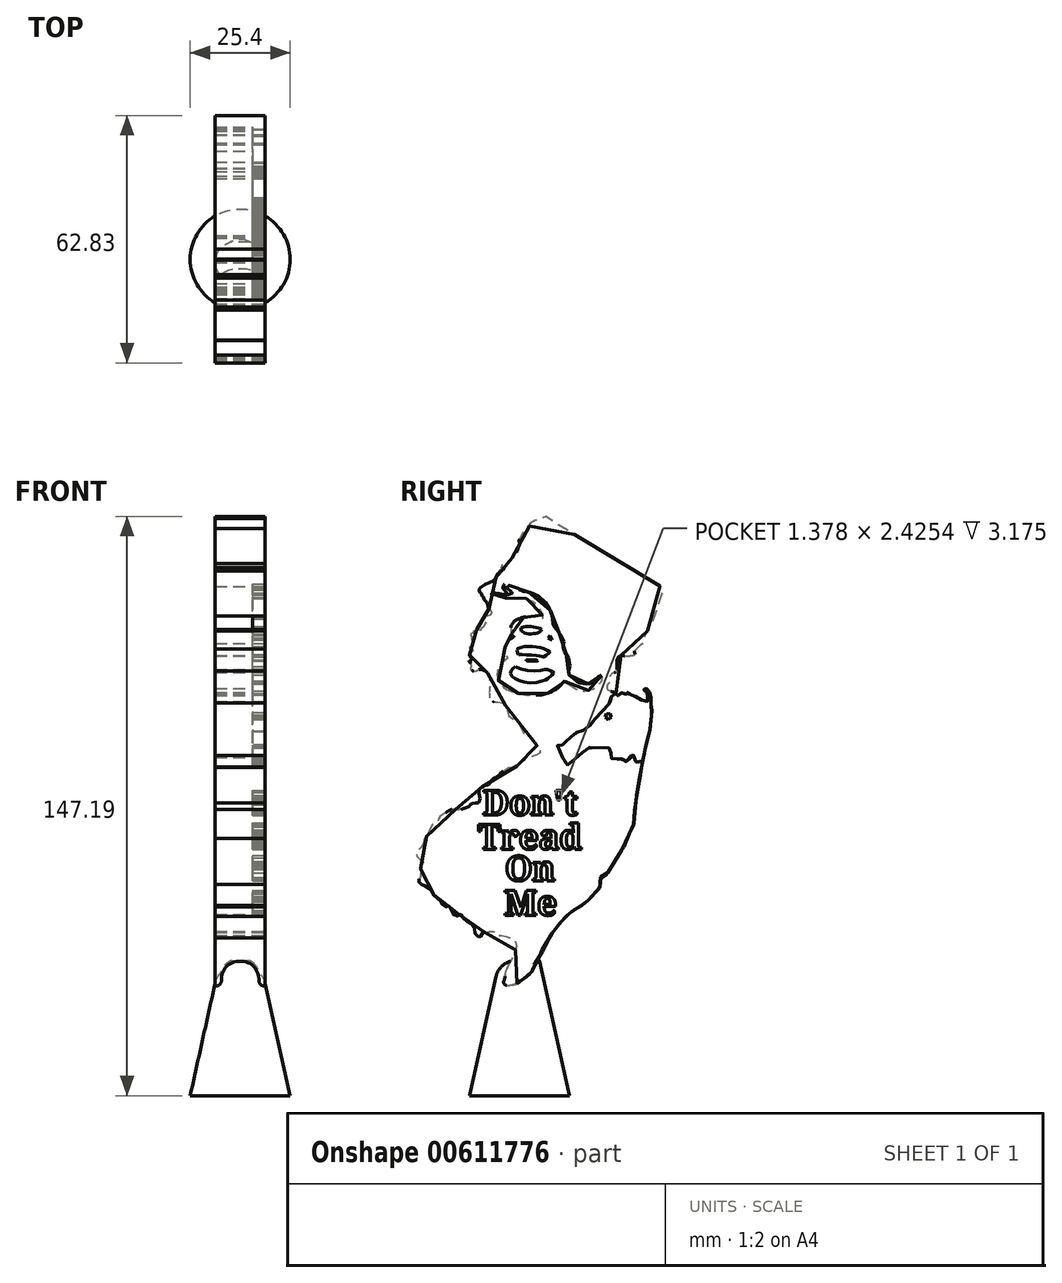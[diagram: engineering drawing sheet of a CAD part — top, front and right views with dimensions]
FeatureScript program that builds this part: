
annotation { "Feature Type Name" : "Feature", "Feature Type Description" : "" }
export const myFeature = defineFeature(function(context is Context, id is Id, definition is map)
    precondition{}
    {
        {
            var Q0;
            Q0=qCreatedBy(makeId("Right.planeOp"),FACE);
            var sketch = newSketch(context, id + "F0", { "sketchPlane" : qUnion([Q0])});
            skLineSegment(sketch, "E0", {"start": v(0, 0) * mm, "end": v(0, 31.75) * mm, "construction": true});
            skFitSpline(sketch, "E1", {"points": [v(-0.7, 28.43) * mm, v(0, 29.08) * mm, v(0.84, 29.6) * mm, v(2.15, 30.47) * mm, v(3.1, 31.63) * mm, v(4.2, 34.04) * mm, v(6.01, 36.44) * mm, v(5.65, 36.95) * mm, v(8.32, 41.31) * mm, v(9.58, 43.23) * mm, v(11.1, 44.75) * mm, v(11.86, 45.66) * mm, v(12.67, 46.31) * mm, v(13.5, 47) * mm, v(14.3, 47.4) * mm, v(15.14, 48.06) * mm, v(17, 48.86) * mm, v(17.25, 49.6) * mm, v(17.98, 50.14) * mm, v(21.04, 53.96) * mm, v(21.04, 54.73) * mm, v(20.57, 55.5) * mm, v(20.93, 56) * mm, v(22.02, 56.19) * mm, v(22.57, 56.95) * mm, v(23.74, 58.6) * mm, v(24.36, 59.83) * mm, v(24.98, 61.03) * mm, v(25.96, 62.3) * mm, v(27.42, 65.3) * mm, v(28.07, 67.08) * mm, v(28.7, 68) * mm, v(29.1, 69.92) * mm, v(29.28, 72.84) * mm, v(29.57, 74.3) * mm, v(29.57, 75.6) * mm, v(29.93, 77.14) * mm, v(30.44, 80.56) * mm, v(30.85, 82.31) * mm, v(31.32, 85.37) * mm, v(31.83, 87.6) * mm, v(32.27, 89.63) * mm, v(33.14, 93.06) * mm, v(33.32, 94.7) * mm, v(33.58, 96.92) * mm, v(33.54, 98.56) * mm, v(33.36, 100.24) * mm, v(33.32, 101.88) * mm, v(32.78, 102.82) * mm, v(32.23, 103.4) * mm, v(31.76, 103.44) * mm, v(31.57, 103.04) * mm, v(32.16, 102.57) * mm, v(32.52, 101.77) * mm, v(32.56, 100.64) * mm, v(32.56, 100.2) * mm, v(31.06, 100.5) * mm, v(29.28, 101.55) * mm, v(28.55, 101.7) * mm, v(28, 102.1) * mm, v(27.56, 102.2) * mm, v(27.53, 102.46) * mm, v(27.1, 102.02) * mm, v(25.85, 102.35) * mm, v(25.38, 101.91) * mm, v(24.87, 101.66) * mm, v(24.61, 102.06) * mm, v(23.85, 102.53) * mm, v(22.68, 102.93) * mm, v(22.32, 104.17) * mm, v(23.15, 105.41) * mm, v(23.15, 106.32) * mm, v(23.04, 106.69) * mm, v(23.88, 107.52) * mm, v(24.47, 107.6) * mm, v(24.72, 108.29) * mm, v(24.83, 110.95) * mm, v(25.63, 111.79) * mm, v(26.65, 111.75) * mm, v(27.3, 111.71) * mm, v(29.31, 112.08) * mm, v(29.28, 112.44) * mm, v(29.28, 113.1) * mm, v(30.63, 114.08) * mm, v(31.14, 114.88) * mm, v(31.72, 114.88) * mm, v(31.61, 115.47) * mm, v(31.83, 115.98) * mm, v(31.9, 116.74) * mm, v(32.3, 117.83) * mm, v(33.03, 119.1) * mm, v(33.03, 119.44) * mm, v(33.43, 119.7) * mm, v(34.05, 121.11) * mm, v(34.5, 122.39) * mm, v(35.26, 123.96) * mm, v(35.7, 126.21) * mm, v(36.28, 127.93) * mm, v(36.5, 129.38) * mm, v(36.24, 129.35) * mm, v(35, 129.82) * mm, v(25.52, 135.5) * mm, v(25.01, 135.72) * mm, v(18.6, 139.62) * mm, v(17.58, 140.1) * mm, v(16.56, 140.93) * mm, v(15.8, 141.3) * mm, v(10.58, 144.8) * mm, v(9.78, 145.09) * mm, v(6.53, 147.16) * mm, v(6.02, 147.05) * mm, v(5.51, 146.84) * mm, v(5.44, 146.62) * mm, v(4.1, 146.65) * mm, v(3.94, 146.33) * mm, v(3.65, 145.7) * mm, v(2.82, 145.52) * mm, v(2.6, 145.3) * mm, v(2.6, 144.8) * mm, v(2.05, 144.5) * mm, v(1.9, 144.14) * mm, v(1.54, 144.1) * mm, v(0.7, 142.57) * mm, v(0.63, 142.03) * mm, v(0.2, 141.7) * mm, v(-0.16, 140.82) * mm, v(0, 140.4) * mm, v(0, 139.9) * mm, v(-0.3, 139.4) * mm, v(-0.83, 137.9) * mm, v(-1.3, 137.8) * mm, v(-1.43, 137.29) * mm, v(-2.2, 136.32) * mm, v(-2.65, 135.82) * mm, v(-3.19, 135.57) * mm, v(-3.32, 135.32) * mm, v(-3.7, 135.16) * mm, v(-4.25, 135.07) * mm, v(-4.77, 133.97) * mm, v(-4.56, 133.93) * mm, v(-4.1, 134.05) * mm, v(-3.9, 134.18) * mm, v(-3.96, 133.85) * mm, v(-4.56, 133.35) * mm, v(-4.92, 133.3) * mm, v(-5.25, 132.71) * mm, v(-5.62, 132.58) * mm, v(-5.74, 132.27) * mm, v(-6.2, 131.24) * mm, v(-7.13, 130.66) * mm, v(-9.1, 129.7) * mm, v(-9.86, 129.13) * mm, v(-10.27, 128.62) * mm, v(-10.1, 127.85) * mm, v(-9.75, 127.66) * mm, v(-9.58, 127.03) * mm, v(-9.23, 126.81) * mm, v(-9.12, 126.24) * mm, v(-8.09, 124.94) * mm, v(-8.06, 124.13) * mm, v(-7.65, 123.79) * mm, v(-7.11, 122.96) * mm, v(-7.15, 122.42) * mm, v(-7.67, 121.9) * mm, v(-8.41, 121.92) * mm, v(-8.87, 121.56) * mm, v(-8.43, 121) * mm, v(-8.35, 120.5) * mm, v(-8.87, 119.95) * mm, v(-8.9, 119.52) * mm, v(-9.15, 119.04) * mm, v(-9.56, 118.93) * mm, v(-9.86, 118.65) * mm, v(-10.06, 118.18) * mm, v(-10.64, 118.18) * mm, v(-11.1, 118.33) * mm, v(-11.45, 118.35) * mm, v(-11.62, 118.41) * mm, v(-11.77, 118.02) * mm, v(-11.9, 117.48) * mm, v(-12.38, 117.3) * mm, v(-12.5, 116.96) * mm, v(-12.07, 116.23) * mm, v(-12.57, 115) * mm, v(-12.77, 113.95) * mm, v(-12.62, 113.5) * mm, v(-12.12, 113.52) * mm, v(-11.75, 113.28) * mm, v(-12.03, 112.85) * mm, v(-12.55, 112.3) * mm, v(-12.75, 111.87) * mm, v(-12.53, 111.57) * mm, v(-12.33, 111.2) * mm, v(-12.18, 110.83) * mm, v(-12.49, 110.46) * mm, v(-12.83, 110.4) * mm, v(-12.55, 109.97) * mm, v(-12.33, 109.73) * mm, v(-12.42, 108.75) * mm, v(-12.38, 108.25) * mm, v(-11.66, 107.9) * mm, v(-10.84, 108.02) * mm, v(-10.38, 108.28) * mm, v(-9.47, 108.21) * mm, v(-8.67, 107.76) * mm, v(-7.63, 106.52) * mm, v(-7.65, 104.92) * mm, v(-7.37, 104.44) * mm, v(-7.7, 103.31) * mm, v(-7.63, 102.7) * mm, v(-7.72, 102.34) * mm, v(-7.59, 102) * mm, v(-7.54, 100.87) * mm, v(-6.07, 99.85) * mm, v(-5.79, 99.9) * mm, v(-4.94, 100.13) * mm, v(-3.62, 99.28) * mm, v(-3.6, 98.92) * mm, v(-3.2, 98.07) * mm, v(-3.08, 97.25) * mm, v(-2.69, 96.4) * mm, v(-1.63, 95.65) * mm, v(-0.5, 94.97) * mm, v(0.26, 93.7) * mm, v(0.74, 92.44) * mm, v(2.51, 91.33) * mm, v(4.14, 89.17) * mm, v(4.9, 88.67) * mm, v(5.33, 87.3) * mm, v(4.72, 86.7) * mm, v(4.18, 86.61) * mm, v(3.77, 86.44) * mm, v(3.53, 86.29) * mm, v(3.18, 85.96) * mm, v(2.53, 86) * mm, v(1.78, 86.37) * mm, v(1.26, 85.68) * mm, v(1.08, 84.92) * mm, v(0.39, 84.68) * mm, v(0, 84.06) * mm, v(-0.83, 83.7) * mm, v(-2, 83.4) * mm, v(-2.4, 83.47) * mm, v(-3.58, 82.73) * mm, v(-4.62, 82.06) * mm, v(-5.14, 81.35) * mm, v(-5.83, 80.91) * mm, v(-6.61, 80.7) * mm, v(-6.98, 80.29) * mm, v(-7.34, 79.59) * mm, v(-8.05, 79.04) * mm, v(-8.9, 78.78) * mm, v(-9.63, 78.35) * mm, v(-10.2, 77.89) * mm, v(-10.3, 77.27) * mm, v(-10.25, 76.33) * mm, v(-10, 75.78) * mm, v(-10.07, 75.16) * mm, v(-10.32, 74.51) * mm, v(-11.03, 74.35) * mm, v(-12.14, 74.26) * mm, v(-12.5, 73.9) * mm, v(-13.12, 73.37) * mm, v(-15, 72.72) * mm, v(-16.22, 72.65) * mm, v(-16.98, 72.75) * mm, v(-17.85, 72.5) * mm, v(-18.7, 71.94) * mm, v(-20.63, 70.54) * mm, v(-20.63, 70.27) * mm, v(-20.5, 70.1) * mm, v(-20.7, 69.76) * mm, v(-21.34, 69.58) * mm, v(-21.92, 69.05) * mm, v(-22.5, 68.36) * mm, v(-22.88, 67.47) * mm, v(-23.18, 66.6) * mm, v(-23.78, 65.65) * mm, v(-23.9, 65.33) * mm, v(-24.24, 65.31) * mm, v(-24.33, 64.7) * mm, v(-24.81, 63.27) * mm, v(-25.82, 62.42) * mm, v(-26.14, 61.98) * mm, v(-26.28, 61.27) * mm, v(-25.77, 60.54) * mm, v(-25.02, 59.8) * mm, v(-24.56, 59.53) * mm, v(-24.44, 59.14) * mm, v(-24.76, 58.17) * mm, v(-25.15, 57.6) * mm, v(-25.02, 57.19) * mm, v(-25.1, 55.9) * mm, v(-25, 55.67) * mm, v(-25.5, 55.49) * mm, v(-25.61, 54.84) * mm, v(-25.68, 54.6) * mm, v(-25.52, 54.1) * mm, v(-25.38, 53.74) * mm, v(-24.53, 53.7) * mm, v(-24.12, 53.4) * mm, v(-23.7, 52.9) * mm, v(-22.67, 52.53) * mm, v(-22.47, 52.2) * mm, v(-22, 51.36) * mm, v(-21.5, 50.57) * mm, v(-20.95, 50.1) * mm, v(-20.3, 49.82) * mm, v(-20.01, 49.27) * mm, v(-19.9, 48.83) * mm, v(-18.95, 48.14) * mm, v(-18.73, 47.96) * mm, v(-18.56, 48.19) * mm, v(-18.36, 48.3) * mm, v(-17.62, 48.07) * mm, v(-17.42, 47.45) * mm, v(-16.87, 46.1) * mm, v(-16.06, 45.5) * mm, v(-15.67, 45.94) * mm, v(-14.8, 46) * mm, v(-14.39, 45.6) * mm, v(-14.25, 44.86) * mm, v(-13.2, 44.17) * mm, v(-12.3, 43.62) * mm, v(-11.5, 42.75) * mm, v(-11.4, 41.85) * mm, v(-11.15, 40.87) * mm, v(-10.41, 40.34) * mm, v(-10.14, 40.09) * mm, v(-9.86, 40.54) * mm, v(-9.43, 41.3) * mm, v(-8.94, 41.6) * mm, v(-8.25, 41.5) * mm, v(-7.43, 41.74) * mm, v(-6.58, 41.74) * mm, v(-6.23, 41.7) * mm, v(-6.14, 40.82) * mm, v(-4.86, 40.75) * mm, v(-3.34, 40.43) * mm, v(-2.33, 40.04) * mm, v(-1.69, 40.02) * mm, v(-1.07, 39.14) * mm, v(-0.84, 37.84) * mm, v(-1.63, 35.4) * mm, v(-2.52, 33.73) * mm, v(-3.3, 32.02) * mm, v(-3.62, 30.89) * mm, v(-3.75, 30) * mm, v(-3.93, 29.3) * mm, v(-4.06, 28.66) * mm, v(-3.62, 28.12) * mm, v(-2.93, 27.92) * mm, v(-1.76, 28.12) * mm, v(-0.7, 28.43) * mm]});
            skSolve(sketch);
        }
        {
            var Q0;
            Q0=makeQuery(id+"F0.imprint","IMPRINT",FACE,{"disambiguationData":[TD([[makeQuery(id+"F0.imprint","IMPRINT",EDGE,{"derivedFrom":sQuery(id+"F0.wireOp",EDGE,"E1")}),1.0]])]});
            extrude(context, id + "F1", {"entities" : qUnion([Q0]), "depth" : 6.35 * mm, "offsetDistance" : 25.4 * mm, "hasSecondDirection" : true, "secondDirectionOppositeDirection" : true, "secondDirectionDepth" : 6.35 * mm});
        }
        {
            var Q0;
            Q0=qCreatedBy(makeId("Right.planeOp"),FACE);
            cPlane(context, id + "F2", {"entities" : qUnion([Q0]), "cplaneType" : CPlaneType.OFFSET, "offset" : 6.35 * mm, "width" : 152.4 * mm, "height" : 152.4 * mm});
        }
        {
            var Q0;
            Q0=qCreatedBy(id+"F2.planeOp",FACE);
            var sketch = newSketch(context, id + "F3", { "sketchPlane" : qUnion([Q0])});
            skFitSpline(sketch, "E2", {"points": [v(11.72, 84) * mm, v(13.04, 84.42) * mm, v(13.83, 85.4) * mm, v(14.67, 85.93) * mm, v(15.8, 87.03) * mm, v(17.04, 87.97) * mm, v(17.2, 88.39) * mm, v(22.52, 88.28) * mm, v(22.86, 88.28) * mm, v(22.86, 87.37) * mm, v(23.16, 87.22) * mm, v(23.5, 86.58) * mm, v(23.54, 86.09) * mm, v(23.35, 85.7) * mm, v(24.03, 85.44) * mm, v(25.2, 85.52) * mm, v(26.45, 85.37) * mm, v(27.01, 84.91) * mm, v(27.66, 85.6) * mm, v(28.52, 86.43) * mm, v(29.05, 86.31) * mm, v(29.1, 85.44) * mm, v(29.58, 84.8) * mm, v(30.07, 84.57) * mm, v(30.87, 84.91) * mm, v(31.55, 85) * mm, v(33.55, 84.91) * mm, v(34.63, 105.23) * mm, v(30.42, 104.69) * mm, v(24.7, 103.18) * mm, v(24.46, 102.15) * mm, v(24, 101.96) * mm, v(23.6, 101.82) * mm, v(23.28, 101.34) * mm, v(23.25, 100.03) * mm, v(22.74, 99.5) * mm, v(18.94, 95.47) * mm, v(18.24, 94.8) * mm, v(17.86, 94.15) * mm, v(17.68, 93.73) * mm, v(17.4, 93.46) * mm, v(15.29, 92.38) * mm, v(14.97, 92.44) * mm, v(14.51, 92.41) * mm, v(14.49, 91.9) * mm, v(14.24, 91.82) * mm, v(12.9, 90.99) * mm, v(12.2, 90.59) * mm, v(11.83, 90.05) * mm, v(11.54, 89.57) * mm, v(11.48, 89.14) * mm, v(11, 89.17) * mm, v(10.7, 89) * mm, v(10.2, 88.84) * mm, v(9.85, 88.98) * mm, v(9.63, 88.95) * mm, v(9.93, 87.99) * mm, v(11.37, 84.6) * mm, v(11.72, 84) * mm]});
            skSolve(sketch);
        }
        {
            var Q0;
            Q0=makeQuery(id+"F3.imprint","IMPRINT",FACE,{"disambiguationData":[TD([[makeQuery(id+"F3.imprint","IMPRINT",EDGE,{"derivedFrom":sQuery(id+"F3.wireOp",EDGE,"E2")}),1.0]])]});
            extrude(context, id + "F4", {"entities" : qUnion([Q0]), "operationType" : NewBodyOperationType.REMOVE, "oppositeDirection" : true, "depth" : 3.17 * mm, "offsetDistance" : 25.4 * mm});
        }
        {
            var Q0;
            Q0=qCreatedBy(id+"F2.planeOp",FACE);
            var sketch = newSketch(context, id + "F5", { "sketchPlane" : qUnion([Q0])});
            skPoint(sketch, "E3.0.midPoint", {"position": v(23.32, 96.1) * mm});
            skLineSegment(sketch, "E4", {"start": v(23.13, 95.53) * mm, "end": v(22.9, 96.23) * mm});
            skLineSegment(sketch, "E5", {"start": v(22.53, 97.38) * mm, "end": v(22.3, 96.67) * mm});
            skLineSegment(sketch, "E6", {"start": v(21.93, 95.53) * mm, "end": v(22.53, 95.96) * mm});
            skLineSegment(sketch, "E7", {"start": v(23.5, 96.67) * mm, "end": v(22.76, 96.67) * mm});
            skLineSegment(sketch, "E8", {"start": v(21.56, 96.67) * mm, "end": v(22.16, 96.23) * mm});
            skLineSegment(sketch, "E9.trimOffspring", {"start": v(22.3, 96.67) * mm, "end": v(21.56, 96.67) * mm});
            skLineSegment(sketch, "E10.trimOffspring", {"start": v(22.16, 96.23) * mm, "end": v(21.93, 95.53) * mm});
            skLineSegment(sketch, "E11.trimOffspring", {"start": v(22.53, 95.96) * mm, "end": v(23.13, 95.53) * mm});
            skLineSegment(sketch, "E12.trimOffspring", {"start": v(22.9, 96.23) * mm, "end": v(23.5, 96.67) * mm});
            skLineSegment(sketch, "E13.trimOffspring", {"start": v(22.76, 96.67) * mm, "end": v(22.53, 97.38) * mm});
            skSolve(sketch);
        }
        {
            var Q0;
            Q0=makeQuery(id+"F5.imprint","IMPRINT",FACE,{"disambiguationData":[TD([[makeQuery(id+"F5.imprint","IMPRINT",EDGE,{"derivedFrom":sQuery(id+"F5.wireOp",EDGE,"E4")}),1.0]])]});
            extrude(context, id + "F6", {"entities" : qUnion([Q0]), "operationType" : NewBodyOperationType.ADD, "oppositeDirection" : true, "depth" : 6.35 * mm, "offsetDistance" : 25.4 * mm});
        }
        {
            var Q0;
            Q0=qCreatedBy(id+"F2.planeOp",FACE);
            var sketch = newSketch(context, id + "F7", { "sketchPlane" : qUnion([Q0])});
            skFitSpline(sketch, "E14", {"points": [v(20.83, 106.8) * mm, v(20.25, 106.76) * mm, v(19.82, 106.13) * mm, v(18.86, 105.3) * mm, v(17.88, 104.7) * mm, v(16.64, 104.64) * mm, v(15.2, 104.9) * mm, v(14.22, 105.63) * mm, v(12.33, 107.21) * mm, v(12.46, 107.62) * mm, v(12.76, 109.15) * mm, v(11.98, 112.08) * mm, v(11.02, 113.51) * mm, v(11.22, 114.7) * mm, v(10.87, 116.49) * mm, v(8.63, 119.24) * mm, v(8.53, 119.54) * mm, v(8.2, 122) * mm, v(7.42, 124.02) * mm, v(5.2, 126.7) * mm, v(2.15, 128.03) * mm, v(0.41, 128.2) * mm, v(-0.45, 128.84) * mm, v(-1.18, 129.22) * mm, v(-3.42, 129.95) * mm, v(-3.82, 130.02) * mm, v(-4.08, 129.64) * mm, v(-4.2, 128.99) * mm, v(-4.1, 128.7) * mm, v(-4, 128.9) * mm, v(-3.91, 128.5) * mm, v(-3.65, 129.07) * mm, v(-3.28, 129) * mm, v(-1.93, 127.7) * mm, v(-2.7, 127.37) * mm, v(-3.35, 127.21) * mm, v(-4.77, 127.42) * mm, v(-6.85, 127.68) * mm, v(-7.22, 127.5) * mm, v(-6.9, 127.46) * mm, v(-7.02, 127.19) * mm, v(-6.54, 127.26) * mm, v(-3.52, 126.95) * mm, v(-3.75, 126.75) * mm, v(-3.51, 126.35) * mm, v(-2.32, 126.41) * mm, v(-0.71, 126.5) * mm, v(1.38, 126.35) * mm, v(2.62, 125.94) * mm, v(4.3, 124.78) * mm, v(5.54, 122.77) * mm, v(5.85, 121.18) * mm, v(5.38, 121.22) * mm, v(2.53, 121.6) * mm, v(0.38, 121.4) * mm, v(-1.5, 120.38) * mm, v(-2.24, 118.77) * mm, v(-1.76, 116.94) * mm, v(-1.42, 116.63) * mm, v(-1.72, 116.43) * mm, v(-3.13, 115.2) * mm, v(-3.68, 113.82) * mm, v(-3.4, 111.9) * mm, v(-2.98, 111.21) * mm, v(-3.03, 111.12) * mm, v(-4.1, 110.3) * mm, v(-4.95, 109.2) * mm, v(-5.57, 108.2) * mm, v(-5.72, 106.67) * mm, v(-5.4, 105.42) * mm, v(-4.35, 104) * mm, v(-2.84, 102.98) * mm, v(0.2, 102.05) * mm, v(3.3, 101.77) * mm, v(6.05, 101.94) * mm, v(8.44, 102.77) * mm, v(10.35, 104.19) * mm, v(11.37, 105.35) * mm, v(11.47, 105.26) * mm, v(14, 103.55) * mm, v(15.84, 102.9) * mm, v(18.03, 103.1) * mm, v(19.7, 104.08) * mm, v(20.9, 105.54) * mm, v(20.83, 106.8) * mm]});
            skFitSpline(sketch, "E15", {"points": [v(-1.09, 109.1) * mm, v(-2, 108.22) * mm, v(-2.35, 107.4) * mm, v(-1.88, 106.44) * mm, v(-0.4, 105.57) * mm, v(3, 104.86) * mm, v(6.42, 105.54) * mm, v(7.02, 105.84) * mm, v(8.63, 107.5) * mm, v(8.43, 107.63) * mm, v(6.93, 108.34) * mm, v(5.96, 108.18) * mm, v(1.85, 108.08) * mm, v(-0.85, 108.94) * mm, v(-1.09, 109.1) * mm]});
            skFitSpline(sketch, "E16", {"points": [v(-0.27, 112.02) * mm, v(-0.6, 112.98) * mm, v(-0.57, 113.42) * mm, v(0.27, 113.9) * mm, v(2.1, 114.18) * mm, v(4.4, 114.04) * mm, v(6.38, 113.52) * mm, v(7.7, 112.65) * mm, v(7.56, 112.56) * mm, v(6.18, 111.47) * mm, v(5.83, 111.45) * mm, v(5.2, 111.7) * mm, v(3.32, 111.96) * mm, v(0.37, 112.05) * mm, v(0, 112.02) * mm, v(-0.27, 112.02) * mm]});
            skFitSpline(sketch, "E17", {"points": [v(5.54, 118.43) * mm, v(5.27, 117.99) * mm, v(4.41, 117.56) * mm, v(3.17, 117.35) * mm, v(1.85, 117.4) * mm, v(0.93, 117.8) * mm, v(0.37, 118.29) * mm, v(0.29, 118.76) * mm, v(0.67, 119.03) * mm, v(1.91, 119.2) * mm, v(3.47, 119.11) * mm, v(5.02, 118.75) * mm, v(5.54, 118.43) * mm]});
            skLineSegment(sketch, "E18", {"start": v(7.76, 116.92) * mm, "end": v(7.25, 116.29) * mm});
            skLineSegment(sketch, "E19", {"start": v(7.25, 116.29) * mm, "end": v(8.25, 115.73) * mm});
            skLineSegment(sketch, "E20", {"start": v(8.25, 115.73) * mm, "end": v(7.76, 116.92) * mm});
            skEllipse(sketch, "E21", {"center": v(3.12, 110.56) * mm, "majorRadius": 1.5 * mm, "minorRadius": 0.16 * mm, "majorAxis": v(1, -0.03)});
            skSolve(sketch);
        }
        {
            var Q0;
            Q0=makeQuery(id+"F7.imprint","IMPRINT",FACE,{"disambiguationData":[TD([[makeQuery(id+"F7.imprint","IMPRINT",EDGE,{"derivedFrom":sQuery(id+"F7.wireOp",EDGE,"E14")}),1.0]])]});
            extrude(context, id + "F8", {"entities" : qUnion([Q0]), "operationType" : NewBodyOperationType.REMOVE, "oppositeDirection" : true, "depth" : 3.17 * mm, "offsetDistance" : 25.4 * mm});
        }
        {
            var Q0;
            Q0=qCreatedBy(id+"F2.planeOp",FACE);
            var sketch = newSketch(context, id + "F9", { "sketchPlane" : qUnion([Q0])});
            skText(sketch, "E22", { "text": "Don\'t", "fontName": "NotoSerif-Bold.ttf"});
            skText(sketch, "E23", { "text": "Tread", "fontName": "NotoSerif-Bold.ttf"});
            skText(sketch, "E24", { "text": "On", "fontName": "NotoSerif-Bold.ttf"});
            skText(sketch, "E25", { "text": "Me", "fontName": "NotoSerif-Bold.ttf"});
            const initialGuessF9  = {"E22": [-0.0094, 0.0713, 1, 0, 0.00635], "E23": [-0.01055, 0.06259, 1, 0, 0.00635], "E24": [-0.0037, 0.05459, 1, 0, 0.00635], "E25": [-0.00394, 0.04582, 1, 0, 0.00635]};
            skSetInitialGuess(sketch, initialGuessF9);
            skSolve(sketch);
        }
        {
            var Q0;
            Q0 = qSketchRegion(id + "F9", true);
            extrude(context, id + "F10", {"entities" : qUnion([Q0]), "operationType" : NewBodyOperationType.REMOVE, "oppositeDirection" : true, "depth" : 3.17 * mm, "offsetDistance" : 25.4 * mm});
        }
        {
            var Q0;
            Q0=qCreatedBy(makeId("Right.planeOp"),FACE);
            var sketch = newSketch(context, id + "F11", { "sketchPlane" : qUnion([Q0])});
            skLineSegment(sketch, "E26", {"start": v(0, 0) * mm, "end": v(0, 34.3) * mm});
            skLineSegment(sketch, "E27", {"start": v(0, 34.3) * mm, "end": v(5.08, 34.3) * mm});
            skLineSegment(sketch, "E28", {"start": v(5.08, 34.3) * mm, "end": v(12.7, 0) * mm});
            skLineSegment(sketch, "E29", {"start": v(12.7, 0) * mm, "end": v(0, 0) * mm});
            skSolve(sketch);
        }
        {
            var Q0;
            Q0=makeQuery(id+"F11.imprint","IMPRINT",FACE,{"disambiguationData":[TD([[makeQuery(id+"F11.imprint","IMPRINT",EDGE,{"derivedFrom":sQuery(id+"F11.wireOp",EDGE,"E26")}),-1.0]])]});
            var Q1;
            Q1=sQuery(id+"F11.wireOp",EDGE,"E26");
            revolve(context, id + "F12", {"operationType" : NewBodyOperationType.ADD, "entities" : qUnion([Q0]), "axis" : qUnion([Q1]), "revolveType" : RevolveType.FULL});
        }
        {
            var Q0;
            Q0=makeQuery(id+"F12.boolean.opBoolean","SPLIT",EDGE,{"disambiguationData":[OD(0.0)],"derivedFrom":makeQuery(id+"F12.opRevolve","SWEPT_EDGE",EDGE,{"disambiguationData":[OSD([sQuery(id+"F11.wireOp",EDGE,"E27"),sQuery(id+"F11.wireOp",EDGE,"E28")])]})});
            fillet(context, id + "F13", {"entities" : qUnion([Q0]), "radius" : 5.08 * mm, "tangentPropagation" : true, "allowEdgeOverflow" : false});
        }
    });
